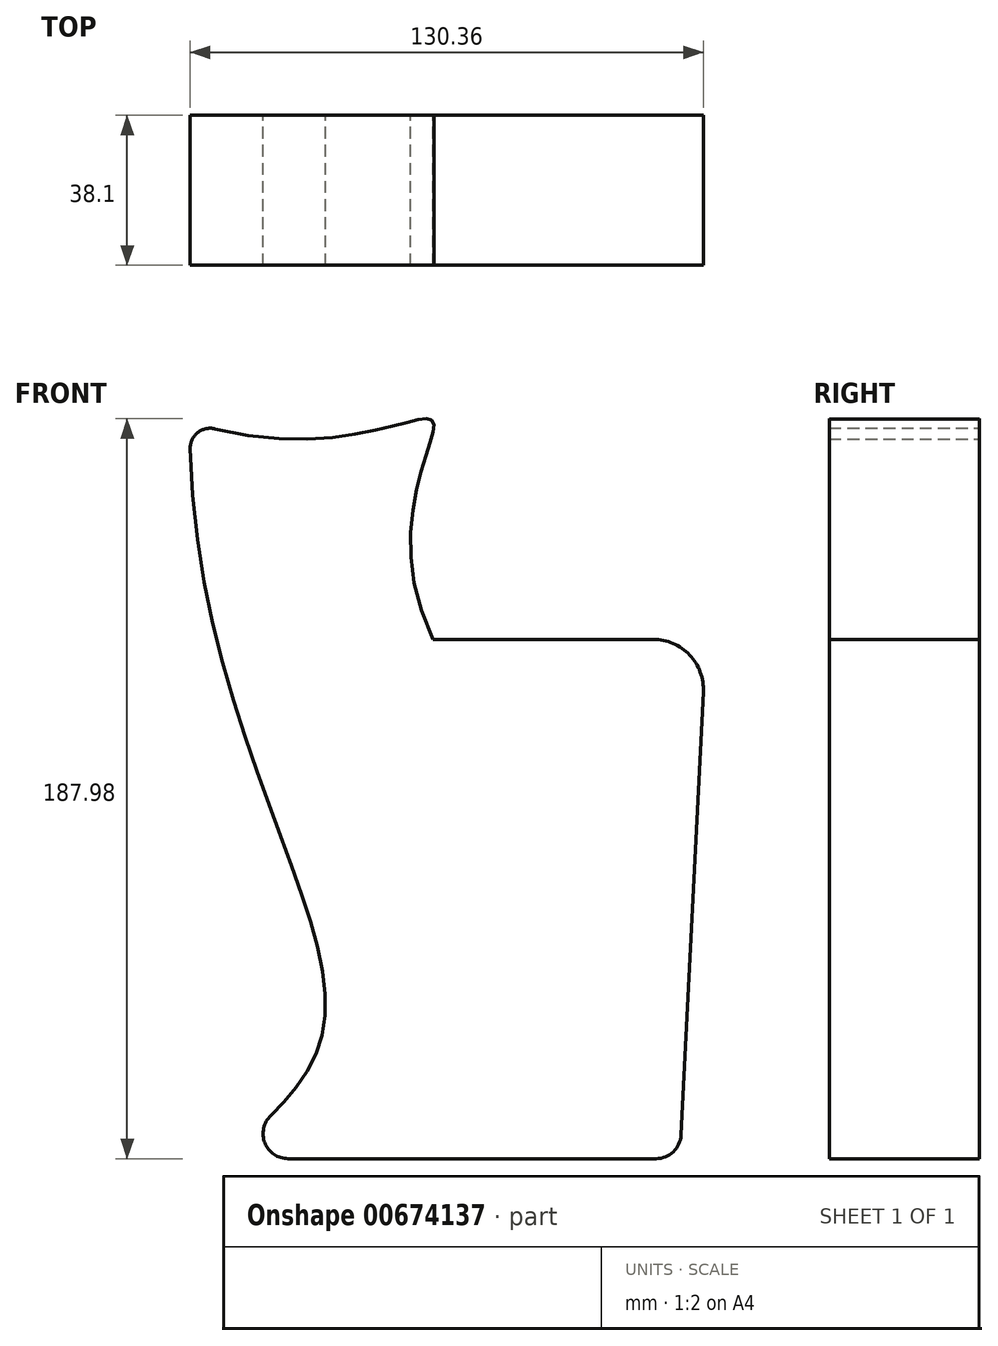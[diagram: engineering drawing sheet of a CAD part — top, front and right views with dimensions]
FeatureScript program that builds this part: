
annotation { "Feature Type Name" : "Feature", "Feature Type Description" : "" }
export const myFeature = defineFeature(function(context is Context, id is Id, definition is map)
    precondition{}
    {
        {
            var Q0;
            Q0=qCreatedBy(makeId("Front.planeOp"),FACE);
            var sketch = newSketch(context, id + "F0", { "sketchPlane" : qUnion([Q0])});
            skLineSegment(sketch, "E0", {"start": v(-36.83, -67.89) * mm, "end": v(56.65, -67.89) * mm});
            skLineSegment(sketch, "E1", {"start": v(62.99, -61.85) * mm, "end": v(68.64, 50.7) * mm});
            skLineSegment(sketch, "E2", {"start": v(55.95, 64.03) * mm, "end": v(0, 64.03) * mm});
            skFitSpline(sketch, "E3", {"points": [v(0, 64.03) * mm, v(0, 119.32) * mm, v(-61.75, 119.32) * mm], "startDerivative": vector(-85.74, 177.34) * mm, "endDerivative": vector(-217.27, 68.82) * mm});
            skFitSpline(sketch, "E4", {"points": [v(-54.7, -67.89) * mm, v(-27.98, -35.43) * mm, v(-61.75, 119.32) * mm], "startDerivative": vector(71.16, 54.27) * mm, "endDerivative": vector(3.4, 338.7) * mm});
            skPoint(sketch, "E5.visualSharp", {"position": v(69.3, 64.03) * mm});
            skArc(sketch, "E5.filletArc", {"start": v(68.64, 50.7) * mm, "mid": v(65.16, 60.08) * mm, "end": v(55.95, 64.03) * mm});
            skPoint(sketch, "E6.visualSharp", {"position": v(62.68, -67.89) * mm});
            skArc(sketch, "E6.filletArc", {"start": v(56.65, -67.89) * mm, "mid": v(61.02, -66.14) * mm, "end": v(62.99, -61.85) * mm});
            skArc(sketch, "E7.filletArc", {"start": v(-41.21, -56.94) * mm, "mid": v(-42.73, -63.9) * mm, "end": v(-36.83, -67.89) * mm});
            skSolve(sketch);
        }
        {
            var Q0;
            Q0 = qSketchRegion(id + "F0", true);
            extrude(context, id + "F1", {"entities" : qUnion([Q0]), "endBound" : BoundingType.SYMMETRIC, "depth" : 38.1 * mm, "offsetDistance" : 25.4 * mm});
        }
        {
            var Q0;
            Q0=makeQuery(id+"F1.opExtrude","SWEPT_EDGE",EDGE,{"disambiguationData":[OSD([sQuery(id+"F0.wireOp",EDGE,"E3"),sQuery(id+"F0.wireOp",EDGE,"E4")])]});
            fillet(context, id + "F2", {"entities" : qUnion([Q0]), "radius" : 5.08 * mm, "tangentPropagation" : true, "allowEdgeOverflow" : false});
        }
    });
